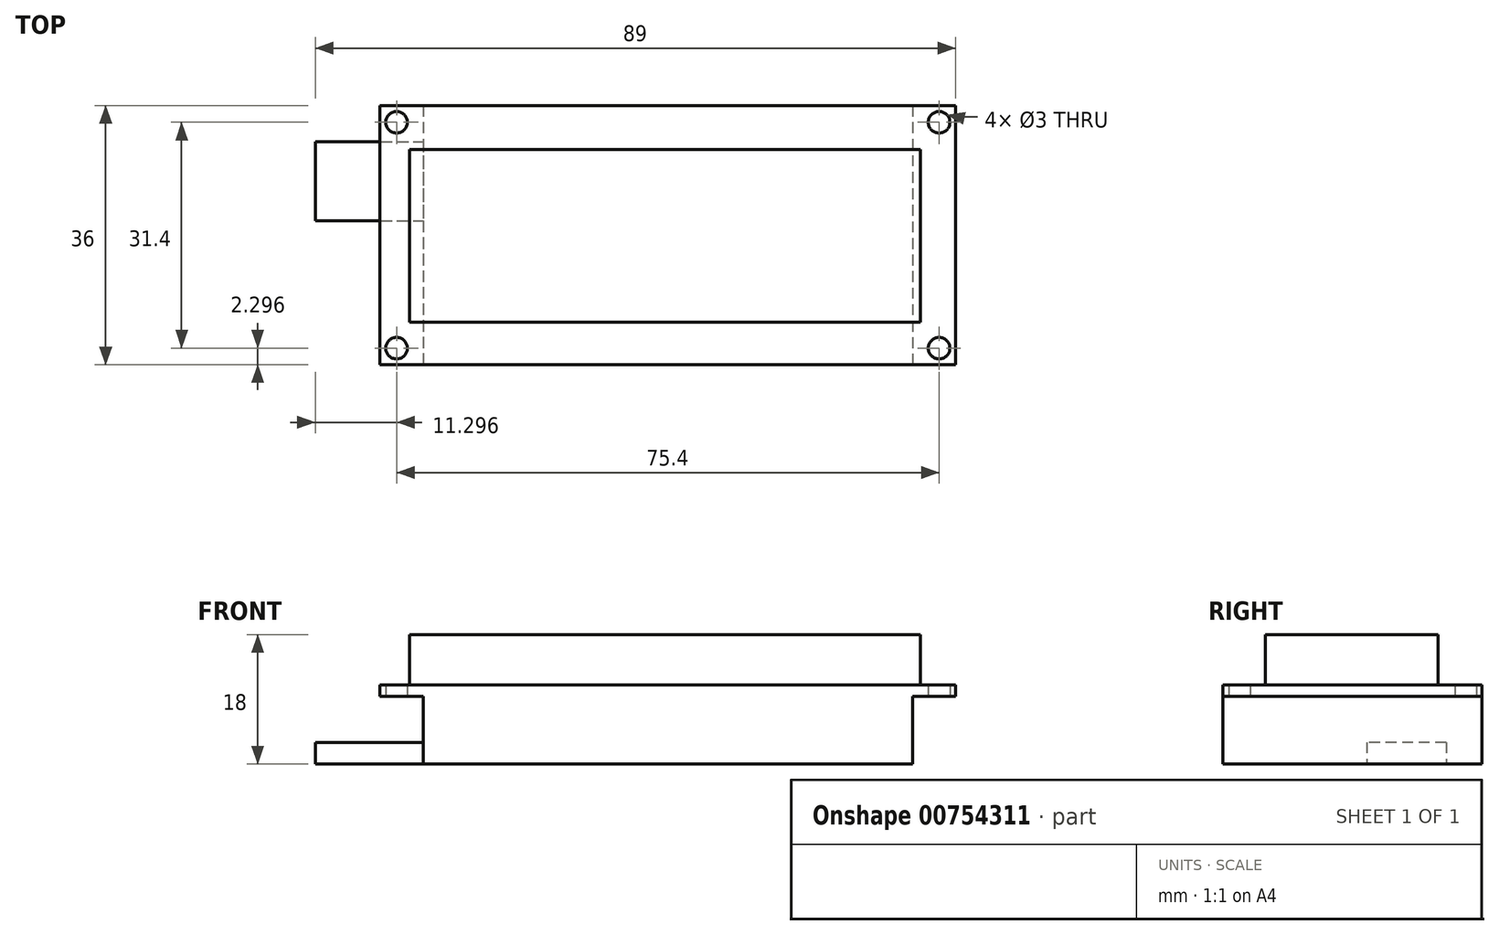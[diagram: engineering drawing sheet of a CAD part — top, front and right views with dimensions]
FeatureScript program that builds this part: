
annotation { "Feature Type Name" : "Feature", "Feature Type Description" : "" }
export const myFeature = defineFeature(function(context is Context, id is Id, definition is map)
    precondition{}
    {
        {
            var Q0;
            Q0=qCreatedBy(makeId("Top.planeOp"),FACE);
            var sketch = newSketch(context, id + "F0", { "sketchPlane" : qUnion([Q0])});
            skLineSegment(sketch, "E0.bottom", {"start": v(-18.37, 31.4) * mm, "end": v(61.63, 31.4) * mm});
            skLineSegment(sketch, "E0.top", {"start": v(-18.37, -4.6) * mm, "end": v(61.63, -4.6) * mm});
            skLineSegment(sketch, "E0.left", {"start": v(-18.37, 31.4) * mm, "end": v(-18.37, -4.6) * mm});
            skLineSegment(sketch, "E0.right", {"start": v(61.63, 31.4) * mm, "end": v(61.63, -4.6) * mm});
            skLineSegment(sketch, "E1.bottom", {"start": v(-14.26, 25.3) * mm, "end": v(56.74, 25.3) * mm});
            skLineSegment(sketch, "E1.top", {"start": v(-14.26, 1.3) * mm, "end": v(56.74, 1.3) * mm});
            skLineSegment(sketch, "E1.left", {"start": v(-14.26, 25.3) * mm, "end": v(-14.26, 1.3) * mm});
            skLineSegment(sketch, "E1.right", {"start": v(56.74, 25.3) * mm, "end": v(56.74, 1.3) * mm});
            skCircle(sketch, "E2", {"center": v(-16.07, 29.1) * mm, "radius": 1.5 * mm});
            skLineSegment(sketch, "E3", {"start": v(-18.37, 13.4) * mm, "end": v(61.63, 13.4) * mm, "construction": true});
            skLineSegment(sketch, "E4", {"start": v(21.63, 31.4) * mm, "end": v(21.63, -4.6) * mm, "construction": true});
            skCircle(sketch, "E5.MirrorC", {"center": v(59.33, 29.1) * mm, "radius": 1.5 * mm});
            skCircle(sketch, "E6.MirrorC", {"center": v(-16.07, -2.3) * mm, "radius": 1.5 * mm});
            skCircle(sketch, "E7.MirrorC", {"center": v(59.33, -2.3) * mm, "radius": 1.5 * mm});
            skSolve(sketch);
        }
        {
            var Q0;
            Q0=makeQuery(id+"F0.imprint","IMPRINT",FACE,{"disambiguationData":[TD([[makeQuery(id+"F0.imprint","IMPRINT",EDGE,{"derivedFrom":sQuery(id+"F0.wireOp",EDGE,"E1.bottom")}),-1.0]])]});
            extrude(context, id + "F1", {"entities" : qUnion([Q0]), "depth" : 8.6 * mm, "offsetDistance" : 25 * mm});
        }
        {
            var Q0;
            Q0=makeQuery(id+"F0.imprint","IMPRINT",FACE,{"disambiguationData":[TD([[makeQuery(id+"F0.imprint","IMPRINT",EDGE,{"derivedFrom":sQuery(id+"F0.wireOp",EDGE,"E0.bottom")}),-1.0]])]});
            extrude(context, id + "F2", {"entities" : qUnion([Q0]), "operationType" : NewBodyOperationType.ADD, "depth" : 1.6 * mm, "offsetDistance" : 25 * mm});
        }
        {
            var Q0;
            Q0=qCreatedBy(makeId("Top.planeOp"),FACE);
            var sketch = newSketch(context, id + "F3", { "sketchPlane" : qUnion([Q0])});
            skLineSegment(sketch, "E8.bottom", {"start": v(71.64, 26.4) * mm, "end": v(43.1, 26.4) * mm});
            skLineSegment(sketch, "E8.top", {"start": v(71.64, 15.4) * mm, "end": v(43.1, 15.4) * mm});
            skLineSegment(sketch, "E8.left", {"start": v(71.64, 26.4) * mm, "end": v(71.64, 15.4) * mm});
            skLineSegment(sketch, "E8.right", {"start": v(43.1, 26.4) * mm, "end": v(43.1, 15.4) * mm});
            skLineSegment(sketch, "E9.bottom", {"start": v(-12.37, 31.4) * mm, "end": v(55.63, 31.4) * mm});
            skLineSegment(sketch, "E9.top", {"start": v(-12.37, -4.6) * mm, "end": v(55.63, -4.6) * mm});
            skLineSegment(sketch, "E9.left", {"start": v(-12.37, 31.4) * mm, "end": v(-12.37, -4.6) * mm});
            skLineSegment(sketch, "E9.right", {"start": v(55.63, 31.4) * mm, "end": v(55.63, -4.6) * mm});
            skSolve(sketch);
        }
        {
            var Q0;
            {var subQ0=sQuery(id+"F3.wireOp",EDGE,"E8.right");Q0=makeQuery(id+"F3.imprint","IMPRINT",FACE,{"disambiguationData":[TD([[makeQuery(id+"F3.imprint","IMPRINT",EDGE,{"derivedFrom":subQ0}),-1.0]])]});}
            var Q1;
            {var subQ0=sQuery(id+"F3.wireOp",EDGE,"E8.right");Q1=makeQuery(id+"F3.imprint","IMPRINT",FACE,{"disambiguationData":[TD([[makeQuery(id+"F3.imprint","IMPRINT",EDGE,{"derivedFrom":subQ0}),1.0]])]});}
            extrude(context, id + "F4", {"entities" : qUnion([Q0, Q1]), "depth" : -9.4 * mm, "offsetDistance" : 25 * mm});
        }
        {
            var Q0;
            Q0=makeQuery(id+"F4.opExtrude","SWEPT_FACE",FACE,{"disambiguationData":[OSD([sQuery(id+"F3.wireOp",EDGE,"E9.left")])]});
            var sketch = newSketch(context, id + "F5", { "sketchPlane" : qUnion([Q0])});
            skLineSegment(sketch, "E10.bottom", {"start": v(-26.4, -6.4) * mm, "end": v(-15.4, -6.4) * mm});
            skLineSegment(sketch, "E10.top", {"start": v(-26.4, -9.4) * mm, "end": v(-15.4, -9.4) * mm});
            skLineSegment(sketch, "E10.left", {"start": v(-26.4, -6.4) * mm, "end": v(-26.4, -9.4) * mm});
            skLineSegment(sketch, "E10.right", {"start": v(-15.4, -6.4) * mm, "end": v(-15.4, -9.4) * mm});
            skSolve(sketch);
        }
        {
            var Q0;
            Q0 = qSketchRegion(id + "F5", true);
            extrude(context, id + "F6", {"entities" : qUnion([Q0]), "operationType" : NewBodyOperationType.ADD, "depth" : 15 * mm, "offsetDistance" : 25 * mm});
        }
    });
